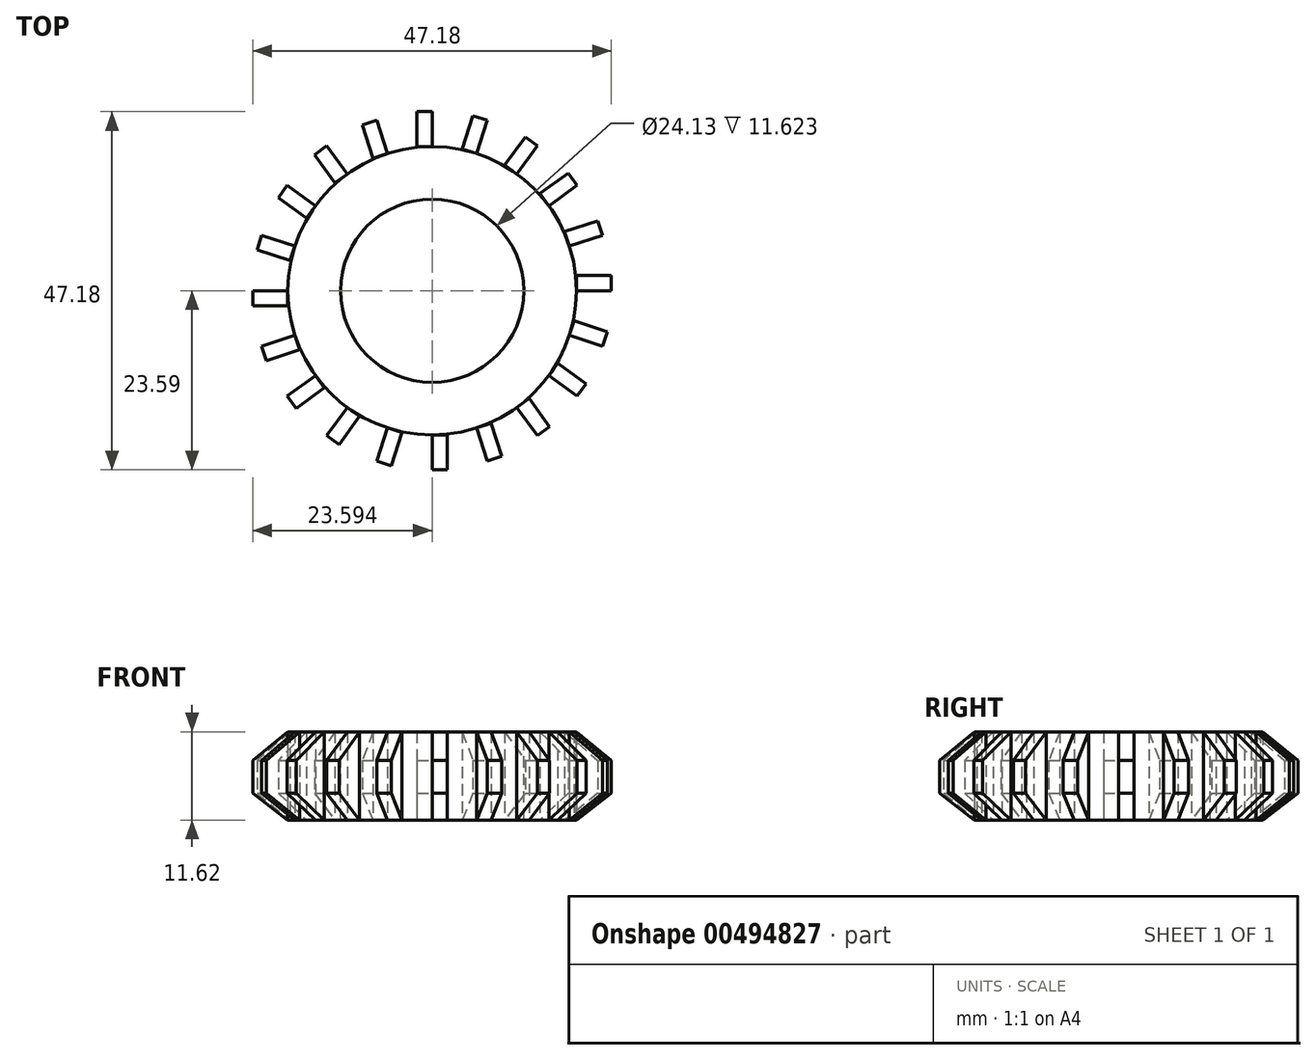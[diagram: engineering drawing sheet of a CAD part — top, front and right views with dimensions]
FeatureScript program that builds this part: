
annotation { "Feature Type Name" : "Feature", "Feature Type Description" : "" }
export const myFeature = defineFeature(function(context is Context, id is Id, definition is map)
    precondition{}
    {
        {
            var Q0;
            Q0=qCreatedBy(makeId("Front.planeOp"),FACE);
            var sketch = newSketch(context, id + "F0", { "sketchPlane" : qUnion([Q0])});
            skLineSegment(sketch, "E0.bottom", {"start": v(0, 0) * mm, "end": v(-9.32, 0) * mm});
            skLineSegment(sketch, "E0.top", {"start": v(0, 31.29) * mm, "end": v(-9.32, 31.29) * mm});
            skLineSegment(sketch, "E0.left", {"start": v(0, 0) * mm, "end": v(0, 31.29) * mm});
            skLineSegment(sketch, "E0.right", {"start": v(-9.32, 0) * mm, "end": v(-9.32, 31.29) * mm});
            skLineSegment(sketch, "E1", {"start": v(3.71, 34.57) * mm, "end": v(3.71, -4.2) * mm});
            skPoint(sketch, "E2.end.orphan", {"position": v(-9.32, 15.64) * mm});
            skLineSegment(sketch, "E3.bottom", {"start": v(-8.35, 11.62) * mm, "end": v(-15.28, 11.62) * mm});
            skLineSegment(sketch, "E3.top", {"start": v(-8.35, 0) * mm, "end": v(-15.28, 0) * mm});
            skLineSegment(sketch, "E3.left", {"start": v(-8.35, 11.62) * mm, "end": v(-8.35, 0) * mm});
            skLineSegment(sketch, "E3.right", {"start": v(-15.28, 11.62) * mm, "end": v(-15.28, 0) * mm});
            skLineSegment(sketch, "E4", {"start": v(-15.28, 11.62) * mm, "end": v(-19.88, 7.84) * mm});
            skLineSegment(sketch, "E5", {"start": v(-19.88, 7.84) * mm, "end": v(-19.88, 3.52) * mm});
            skLineSegment(sketch, "E6", {"start": v(-19.88, 3.52) * mm, "end": v(-15.28, 0) * mm});
            skSolve(sketch);
        }
        {
            var Q0;
            {var subQ1=sQuery(id+"F0.wireOp",EDGE,"E0.bottom");Q0=makeQuery(id+"F0.imprint","IMPRINT",FACE,{"disambiguationData":[TD([[makeQuery(id+"F0.imprint","IMPRINT",EDGE,{"derivedFrom":subQ1}),-1.0]])]});}
            var Q1;
            {var subQ5=sQuery(id+"F0.wireOp",EDGE,"E3.left");Q1=makeQuery(id+"F0.imprint","IMPRINT",FACE,{"disambiguationData":[TD([[makeQuery(id+"F0.imprint","IMPRINT",EDGE,{"derivedFrom":subQ5}),-1.0]])]});}
            var Q2;
            {var subQ5=sQuery(id+"F0.wireOp",EDGE,"E3.right");Q2=makeQuery(id+"F0.imprint","IMPRINT",FACE,{"disambiguationData":[TD([[makeQuery(id+"F0.imprint","IMPRINT",EDGE,{"derivedFrom":subQ5}),1.0]])]});}
            var Q3;
            Q3=sQuery(id+"F0.wireOp",EDGE,"E1");
            revolve(context, id + "F1", {"entities" : qUnion([Q0, Q1, Q2]), "axis" : qUnion([Q3]), "revolveType" : RevolveType.FULL});
        }
        {
            var Q0;
            Q0=makeQuery(id+"F0.imprint","IMPRINT",FACE,{"disambiguationData":[TD([[makeQuery(id+"F0.imprint","IMPRINT",EDGE,{"derivedFrom":sQuery(id+"F0.wireOp",EDGE,"E3.right")}),-1.0]])]});
            extrude(context, id + "F2", {"entities" : qUnion([Q0]), "depth" : 2 * mm});
        }
        {
            var Q0;
            Q0=makeQuery(id+"F2.opExtrude","SWEPT_BODY",BODY,{"disambiguationData":[OSD([sQuery(id+"F0.wireOp",EDGE,"E3.right"),sQuery(id+"F0.wireOp",EDGE,"E4"),sQuery(id+"F0.wireOp",EDGE,"E5"),sQuery(id+"F0.wireOp",EDGE,"E6")])]});
            var Q1;
            Q1=sQuery(id+"F0.wireOp",EDGE,"E1");
            circularPattern(context, id + "F3", {"entities" : qUnion([Q0]), "axis" : qUnion([Q1]), "angle" : 360 * degree, "instanceCount" : 20, "equalSpace" : true});
        }
    });
